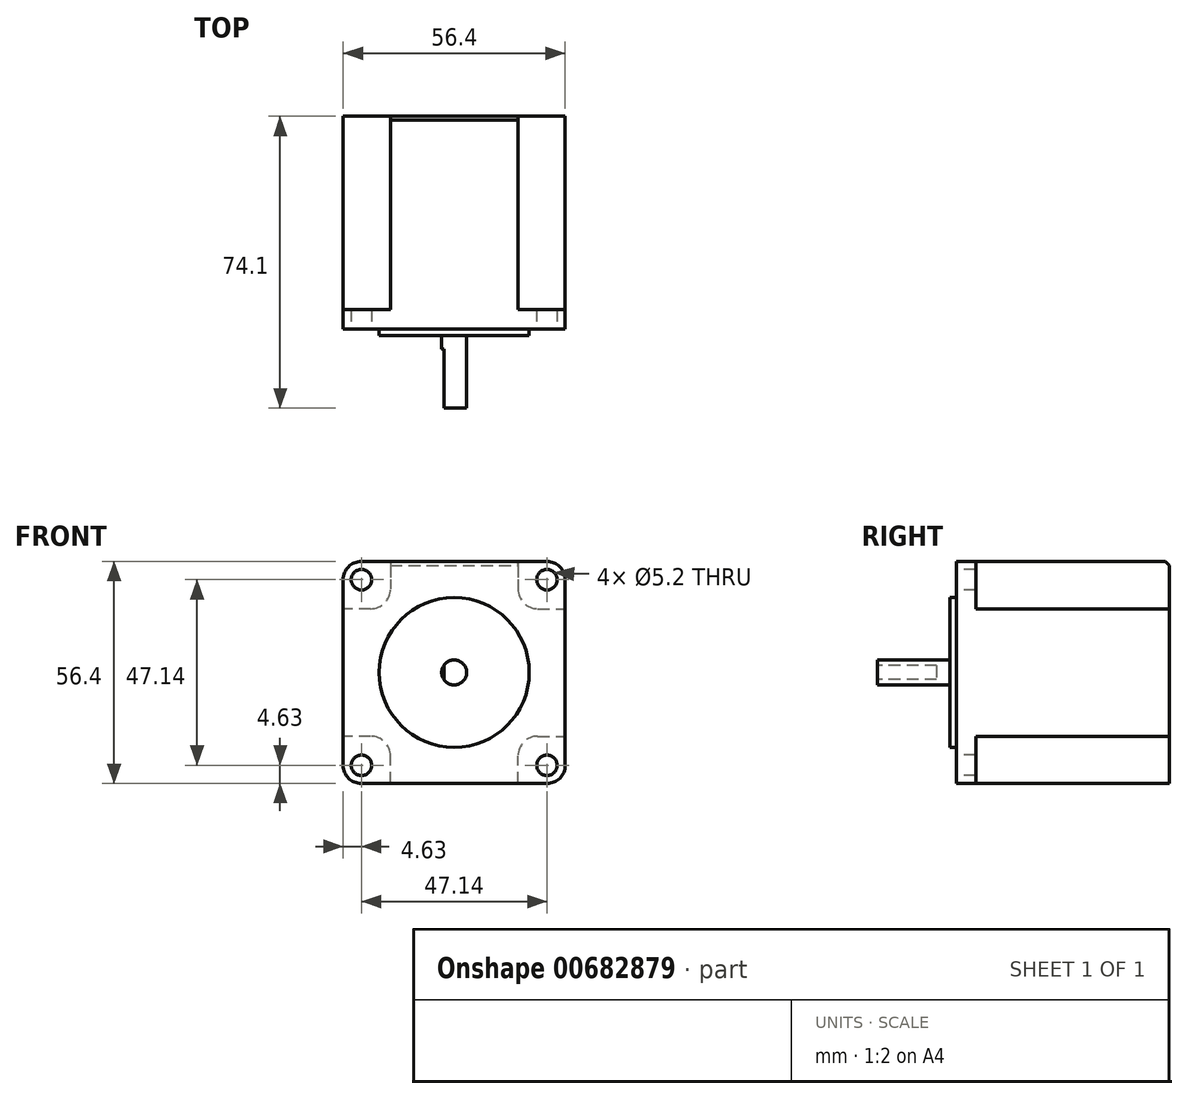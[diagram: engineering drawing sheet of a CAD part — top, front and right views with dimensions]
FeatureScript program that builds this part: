
annotation { "Feature Type Name" : "Feature", "Feature Type Description" : "" }
export const myFeature = defineFeature(function(context is Context, id is Id, definition is map)
    precondition{}
    {
        {
            var Q0;
            Q0=qCreatedBy(makeId("Front.planeOp"),FACE);
            var sketch = newSketch(context, id + "F0", { "sketchPlane" : qUnion([Q0])});
            skLineSegment(sketch, "E0.bottom", {"start": v(28.2, 28.2) * mm, "end": v(-28.2, 28.2) * mm});
            skLineSegment(sketch, "E0.top", {"start": v(28.2, -28.2) * mm, "end": v(-28.2, -28.2) * mm});
            skLineSegment(sketch, "E0.left", {"start": v(28.2, 28.2) * mm, "end": v(28.2, -28.2) * mm});
            skLineSegment(sketch, "E0.right", {"start": v(-28.2, 28.2) * mm, "end": v(-28.2, -28.2) * mm});
            skPoint(sketch, "E0.middle", {"position": v(0, 0) * mm});
            skSolve(sketch);
        }
        {
            var Q0;
            Q0 = qSketchRegion(id + "F0", true);
            extrude(context, id + "F1", {"entities" : qUnion([Q0]), "oppositeDirection" : true, "depth" : 54.1 * mm, "offsetDistance" : 25 * mm});
        }
        {
            var Q0;
            Q0=makeQuery(id+"F1.opExtrude","CAP_FACE",FACE,{"disambiguationData":[OSD([sQuery(id+"F0.wireOp",EDGE,"E0.bottom"),sQuery(id+"F0.wireOp",EDGE,"E0.top"),sQuery(id+"F0.wireOp",EDGE,"E0.left"),sQuery(id+"F0.wireOp",EDGE,"E0.right")])],"isStart":true});
            var sketch = newSketch(context, id + "F2", { "sketchPlane" : qUnion([Q0])});
            skCircle(sketch, "E1", {"center": v(0, 0) * mm, "radius": 19.05 * mm});
            skSolve(sketch);
        }
        {
            var Q0;
            Q0 = qSketchRegion(id + "F2", true);
            extrude(context, id + "F3", {"entities" : qUnion([Q0]), "operationType" : NewBodyOperationType.ADD, "depth" : 1.6 * mm, "offsetDistance" : 25 * mm});
        }
        {
            var Q0;
            Q0=makeQuery(id+"F1.opExtrude","CAP_FACE",FACE,{"disambiguationData":[OSD([sQuery(id+"F0.wireOp",EDGE,"E0.bottom"),sQuery(id+"F0.wireOp",EDGE,"E0.top"),sQuery(id+"F0.wireOp",EDGE,"E0.left"),sQuery(id+"F0.wireOp",EDGE,"E0.right")])],"isStart":true});
            var sketch = newSketch(context, id + "F4", { "sketchPlane" : qUnion([Q0])});
            skCircle(sketch, "E2", {"center": v(0, 0) * mm, "radius": 3.17 * mm});
            skSolve(sketch);
        }
        {
            var Q0;
            Q0 = qSketchRegion(id + "F4", true);
            extrude(context, id + "F5", {"entities" : qUnion([Q0]), "operationType" : NewBodyOperationType.ADD, "depth" : 20 * mm, "offsetDistance" : 25 * mm});
        }
        {
            var Q0;
            Q0=makeQuery(id+"F1.opExtrude","CAP_FACE",FACE,{"disambiguationData":[OSD([sQuery(id+"F0.wireOp",EDGE,"E0.bottom"),sQuery(id+"F0.wireOp",EDGE,"E0.top"),sQuery(id+"F0.wireOp",EDGE,"E0.left"),sQuery(id+"F0.wireOp",EDGE,"E0.right")])],"isStart":true});
            var sketch = newSketch(context, id + "F6", { "sketchPlane" : qUnion([Q0])});
            skLineSegment(sketch, "E3", {"start": v(0, 0) * mm, "end": v(58.55, 0) * mm, "construction": true});
            skLineSegment(sketch, "E4", {"start": v(0, 0) * mm, "end": v(0, 77.41) * mm, "construction": true});
            skCircle(sketch, "E5", {"center": v(23.57, 23.57) * mm, "radius": 2.6 * mm});
            skCircle(sketch, "E6.MirrorC", {"center": v(-23.57, 23.57) * mm, "radius": 2.6 * mm});
            skCircle(sketch, "E7.MirrorC", {"center": v(23.57, -23.57) * mm, "radius": 2.6 * mm});
            skCircle(sketch, "E8.MirrorC", {"center": v(-23.57, -23.57) * mm, "radius": 2.6 * mm});
            skSolve(sketch);
        }
        {
            var Q0;
            Q0 = qSketchRegion(id + "F6", true);
            extrude(context, id + "F7", {"entities" : qUnion([Q0]), "operationType" : NewBodyOperationType.REMOVE, "endBound" : BoundingType.THROUGH_ALL, "oppositeDirection" : true, "depth" : 25 * mm, "offsetDistance" : 25 * mm});
        }
        {
            var Q0;
            Q0=makeQuery(id+"F5.opExtrude","CAP_FACE",FACE,{"disambiguationData":[OSD([sQuery(id+"F4.wireOp",EDGE,"E2")])],"isStart":false});
            var sketch = newSketch(context, id + "F8", { "sketchPlane" : qUnion([Q0])});
            skLineSegment(sketch, "E9", {"start": v(0, 0) * mm, "end": v(0, 37.68) * mm, "construction": true});
            skArc(sketch, "E10.0", {"start": v(-2.62, 1.79) * mm, "mid": v(-3.17, 0) * mm, "end": v(-2.62, -1.79) * mm});
            skLineSegment(sketch, "E11", {"start": v(-2.62, 1.79) * mm, "end": v(-2.62, -1.79) * mm});
            skSolve(sketch);
        }
        {
            var Q0;
            Q0 = qSketchRegion(id + "F8", true);
            extrude(context, id + "F9", {"entities" : qUnion([Q0]), "operationType" : NewBodyOperationType.REMOVE, "oppositeDirection" : true, "depth" : 15 * mm, "offsetDistance" : 25 * mm});
        }
        {
            var Q0;
            Q0=makeQuery(id+"F1.opExtrude","SWEPT_EDGE",EDGE,{"disambiguationData":[OSD([sQuery(id+"F0.wireOp",EDGE,"E0.bottom"),sQuery(id+"F0.wireOp",EDGE,"E0.right")])]});
            var Q1;
            Q1=makeQuery(id+"F1.opExtrude","SWEPT_EDGE",EDGE,{"disambiguationData":[OSD([sQuery(id+"F0.wireOp",EDGE,"E0.top"),sQuery(id+"F0.wireOp",EDGE,"E0.right")])]});
            var Q2;
            Q2=makeQuery(id+"F1.opExtrude","SWEPT_EDGE",EDGE,{"disambiguationData":[OSD([sQuery(id+"F0.wireOp",EDGE,"E0.bottom"),sQuery(id+"F0.wireOp",EDGE,"E0.left")])]});
            var Q3;
            Q3=makeQuery(id+"F1.opExtrude","SWEPT_EDGE",EDGE,{"disambiguationData":[OSD([sQuery(id+"F0.wireOp",EDGE,"E0.top"),sQuery(id+"F0.wireOp",EDGE,"E0.left")])]});
            fillet(context, id + "F10", {"entities" : qUnion([Q0, Q1, Q2, Q3]), "radius" : 4.6 * mm, "tangentPropagation" : true, "allowEdgeOverflow" : false});
        }
        {
            var Q0;
            Q0=makeQuery(id+"F1.opExtrude","CAP_FACE",FACE,{"disambiguationData":[OSD([sQuery(id+"F0.wireOp",EDGE,"E0.bottom"),sQuery(id+"F0.wireOp",EDGE,"E0.top"),sQuery(id+"F0.wireOp",EDGE,"E0.left"),sQuery(id+"F0.wireOp",EDGE,"E0.right")])],"isStart":false});
            var sketch = newSketch(context, id + "F11", { "sketchPlane" : qUnion([Q0])});
            skLineSegment(sketch, "E12", {"start": v(0, 0) * mm, "end": v(45.43, 0) * mm, "construction": true});
            skLineSegment(sketch, "E13", {"start": v(0, 0) * mm, "end": v(0, 57.73) * mm, "construction": true});
            skLineSegment(sketch, "E14.bottom", {"start": v(16.2, 28.2) * mm, "end": v(28.2, 28.2) * mm});
            skLineSegment(sketch, "E14.top", {"start": v(16.2, 16.2) * mm, "end": v(28.2, 16.2) * mm});
            skLineSegment(sketch, "E14.left", {"start": v(16.2, 28.2) * mm, "end": v(16.2, 16.2) * mm});
            skLineSegment(sketch, "E14.right", {"start": v(28.2, 28.2) * mm, "end": v(28.2, 16.2) * mm});
            skLineSegment(sketch, "E15.MirrorCS", {"start": v(-16.2, 16.2) * mm, "end": v(-28.2, 16.2) * mm});
            skLineSegment(sketch, "E16.MirrorCS", {"start": v(-16.2, 28.2) * mm, "end": v(-28.2, 28.2) * mm});
            skLineSegment(sketch, "E17.MirrorCS", {"start": v(-16.2, 28.2) * mm, "end": v(-16.2, 16.2) * mm});
            skLineSegment(sketch, "E18.MirrorCS", {"start": v(-28.2, 28.2) * mm, "end": v(-28.2, 16.2) * mm});
            skLineSegment(sketch, "E19.MirrorCS", {"start": v(16.2, -16.2) * mm, "end": v(28.2, -16.2) * mm});
            skLineSegment(sketch, "E20.MirrorCS", {"start": v(16.2, -28.2) * mm, "end": v(28.2, -28.2) * mm});
            skLineSegment(sketch, "E21.MirrorCS", {"start": v(16.2, -28.2) * mm, "end": v(16.2, -16.2) * mm});
            skLineSegment(sketch, "E22.MirrorCS", {"start": v(28.2, -28.2) * mm, "end": v(28.2, -16.2) * mm});
            skLineSegment(sketch, "E23.MirrorCS", {"start": v(-16.2, -16.2) * mm, "end": v(-28.2, -16.2) * mm});
            skLineSegment(sketch, "E24.MirrorCS", {"start": v(-16.2, -28.2) * mm, "end": v(-28.2, -28.2) * mm});
            skLineSegment(sketch, "E25.MirrorCS", {"start": v(-16.2, -28.2) * mm, "end": v(-16.2, -16.2) * mm});
            skLineSegment(sketch, "E26.MirrorCS", {"start": v(-28.2, -28.2) * mm, "end": v(-28.2, -16.2) * mm});
            skSolve(sketch);
        }
        {
            var Q0;
            Q0 = qSketchRegion(id + "F11", true);
            extrude(context, id + "F12", {"entities" : qUnion([Q0]), "operationType" : NewBodyOperationType.REMOVE, "oppositeDirection" : true, "depth" : 49.1 * mm, "offsetDistance" : 25 * mm});
        }
        {
            var Q0;
            Q0=makeQuery(id+"F12.boolean.opBoolean","COPY",EDGE,{"derivedFrom":makeQuery(id+"F12.opExtrude","SWEPT_EDGE",EDGE,{"disambiguationData":[OSD([sQuery(id+"F0.wireOp",EDGE,"E0.bottom"),sQuery(id+"F11.wireOp",EDGE,"E14.bottom"),sQuery(id+"F11.wireOp",EDGE,"E14.left")])]})});
            var Q1;
            Q1=makeQuery(id+"F12.boolean.opBoolean","COPY",EDGE,{"derivedFrom":makeQuery(id+"F12.opExtrude","SWEPT_EDGE",EDGE,{"disambiguationData":[OSD([sQuery(id+"F11.wireOp",EDGE,"E14.top"),sQuery(id+"F11.wireOp",EDGE,"E14.left")])]})});
            var Q2;
            Q2=makeQuery(id+"F12.boolean.opBoolean","COPY",EDGE,{"derivedFrom":makeQuery(id+"F12.opExtrude","SWEPT_EDGE",EDGE,{"disambiguationData":[OSD([sQuery(id+"F0.wireOp",EDGE,"E0.right"),sQuery(id+"F11.wireOp",EDGE,"E14.top"),sQuery(id+"F11.wireOp",EDGE,"E14.right")])]})});
            var Q3;
            Q3=makeQuery(id+"F12.boolean.opBoolean","COPY",EDGE,{"derivedFrom":makeQuery(id+"F12.opExtrude","SWEPT_EDGE",EDGE,{"disambiguationData":[OSD([sQuery(id+"F0.wireOp",EDGE,"E0.bottom"),sQuery(id+"F11.wireOp",EDGE,"E16.MirrorCS"),sQuery(id+"F11.wireOp",EDGE,"E17.MirrorCS")])]})});
            var Q4;
            Q4=makeQuery(id+"F12.boolean.opBoolean","COPY",EDGE,{"derivedFrom":makeQuery(id+"F12.opExtrude","SWEPT_EDGE",EDGE,{"disambiguationData":[OSD([sQuery(id+"F11.wireOp",EDGE,"E15.MirrorCS"),sQuery(id+"F11.wireOp",EDGE,"E17.MirrorCS")])]})});
            var Q5;
            Q5=makeQuery(id+"F12.boolean.opBoolean","COPY",EDGE,{"derivedFrom":makeQuery(id+"F12.opExtrude","SWEPT_EDGE",EDGE,{"disambiguationData":[OSD([sQuery(id+"F0.wireOp",EDGE,"E0.left"),sQuery(id+"F11.wireOp",EDGE,"E15.MirrorCS"),sQuery(id+"F11.wireOp",EDGE,"E18.MirrorCS")])]})});
            var Q6;
            Q6=makeQuery(id+"F12.boolean.opBoolean","COPY",EDGE,{"derivedFrom":makeQuery(id+"F12.opExtrude","SWEPT_EDGE",EDGE,{"disambiguationData":[OSD([sQuery(id+"F0.wireOp",EDGE,"E0.left"),sQuery(id+"F11.wireOp",EDGE,"E23.MirrorCS"),sQuery(id+"F11.wireOp",EDGE,"E26.MirrorCS")])]})});
            var Q7;
            Q7=makeQuery(id+"F12.boolean.opBoolean","COPY",EDGE,{"derivedFrom":makeQuery(id+"F12.opExtrude","SWEPT_EDGE",EDGE,{"disambiguationData":[OSD([sQuery(id+"F11.wireOp",EDGE,"E23.MirrorCS"),sQuery(id+"F11.wireOp",EDGE,"E25.MirrorCS")])]})});
            var Q8;
            Q8=makeQuery(id+"F12.boolean.opBoolean","COPY",EDGE,{"derivedFrom":makeQuery(id+"F12.opExtrude","SWEPT_EDGE",EDGE,{"disambiguationData":[OSD([sQuery(id+"F0.wireOp",EDGE,"E0.top"),sQuery(id+"F11.wireOp",EDGE,"E24.MirrorCS"),sQuery(id+"F11.wireOp",EDGE,"E25.MirrorCS")])]})});
            var Q9;
            Q9=makeQuery(id+"F12.boolean.opBoolean","COPY",EDGE,{"derivedFrom":makeQuery(id+"F12.opExtrude","SWEPT_EDGE",EDGE,{"disambiguationData":[OSD([sQuery(id+"F0.wireOp",EDGE,"E0.top"),sQuery(id+"F11.wireOp",EDGE,"E20.MirrorCS"),sQuery(id+"F11.wireOp",EDGE,"E21.MirrorCS")])]})});
            var Q10;
            Q10=makeQuery(id+"F12.boolean.opBoolean","COPY",EDGE,{"derivedFrom":makeQuery(id+"F12.opExtrude","SWEPT_EDGE",EDGE,{"disambiguationData":[OSD([sQuery(id+"F11.wireOp",EDGE,"E19.MirrorCS"),sQuery(id+"F11.wireOp",EDGE,"E21.MirrorCS")])]})});
            var Q11;
            Q11=makeQuery(id+"F12.boolean.opBoolean","COPY",EDGE,{"derivedFrom":makeQuery(id+"F12.opExtrude","SWEPT_EDGE",EDGE,{"disambiguationData":[OSD([sQuery(id+"F0.wireOp",EDGE,"E0.right"),sQuery(id+"F11.wireOp",EDGE,"E19.MirrorCS"),sQuery(id+"F11.wireOp",EDGE,"E22.MirrorCS")])]})});
            fillet(context, id + "F13", {"entities" : qUnion([Q0, Q1, Q2, Q3, Q4, Q5, Q6, Q7, Q8, Q9, Q10, Q11]), "radius" : 5 * mm, "tangentPropagation" : true, "allowEdgeOverflow" : false});
        }
        {
            var Q0;
            Q0=makeQuery(id+"F1.opExtrude","CAP_EDGE",EDGE,{"disambiguationData":[OSD([sQuery(id+"F0.wireOp",EDGE,"E0.bottom")])],"isStart":false});
            chamfer(context, id + "F14", {"entities" : qUnion([Q0]), "width" : 1 * mm, "tangentPropagation" : true});
        }
    });
